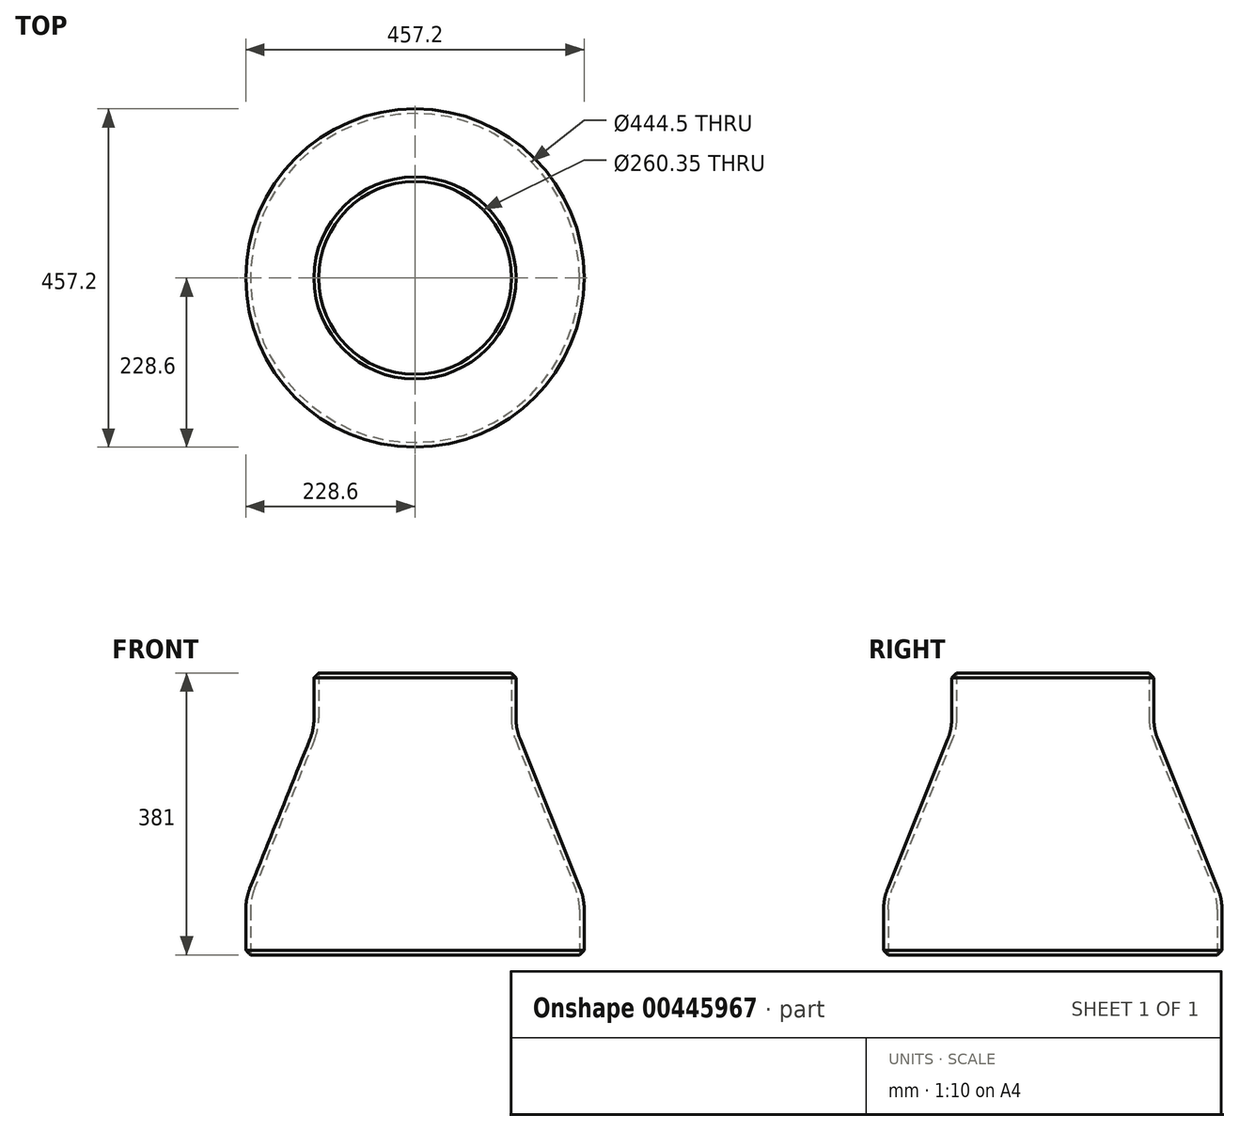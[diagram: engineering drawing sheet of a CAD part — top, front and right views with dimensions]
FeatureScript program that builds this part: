
annotation { "Feature Type Name" : "Feature", "Feature Type Description" : "" }
export const myFeature = defineFeature(function(context is Context, id is Id, definition is map)
    precondition{}
    {
        {
            var Q0;
            Q0=qCreatedBy(makeId("Front.planeOp"),FACE);
            var sketch = newSketch(context, id + "F0", { "sketchPlane" : qUnion([Q0])});
            skLineSegment(sketch, "E0", {"start": v(-130.18, 189.88) * mm, "end": v(-130.18, 128.45) * mm});
            skLineSegment(sketch, "E1", {"start": v(-222.25, -191.12) * mm, "end": v(-222.25, -129.68) * mm});
            skLineSegment(sketch, "E2", {"start": v(-216.73, -101.22) * mm, "end": v(-135.7, 99.98) * mm});
            skLineSegment(sketch, "E3", {"start": v(-136.53, 189.88) * mm, "end": v(-136.53, 128.45) * mm});
            skLineSegment(sketch, "E4", {"start": v(-142.04, 99.98) * mm, "end": v(-223.08, -101.22) * mm});
            skLineSegment(sketch, "E5", {"start": v(-228.6, -129.68) * mm, "end": v(-228.6, -191.12) * mm});
            skPoint(sketch, "E6.visualSharp", {"position": v(-222.25, -114.92) * mm});
            skArc(sketch, "E6.filletArc", {"start": v(-216.73, -101.22) * mm, "mid": v(-220.86, -115.19) * mm, "end": v(-222.25, -129.68) * mm});
            skPoint(sketch, "E7.visualSharp", {"position": v(-228.6, -114.92) * mm});
            skArc(sketch, "E7.filletArc", {"start": v(-223.08, -101.22) * mm, "mid": v(-227.2, -115.19) * mm, "end": v(-228.6, -129.68) * mm});
            skPoint(sketch, "E8.visualSharp", {"position": v(-136.53, 113.68) * mm});
            skArc(sketch, "E8.filletArc", {"start": v(-142.04, 99.98) * mm, "mid": v(-137.92, 113.95) * mm, "end": v(-136.53, 128.45) * mm});
            skPoint(sketch, "E9.visualSharp", {"position": v(-130.18, 113.68) * mm});
            skArc(sketch, "E9.filletArc", {"start": v(-135.7, 99.98) * mm, "mid": v(-131.57, 113.95) * mm, "end": v(-130.18, 128.45) * mm});
            skLineSegment(sketch, "E10", {"start": v(-136.53, 189.88) * mm, "end": v(-130.18, 189.88) * mm});
            skLineSegment(sketch, "E11", {"start": v(-228.6, -191.12) * mm, "end": v(-222.25, -191.12) * mm});
            skSolve(sketch);
        }
        {
            var Q0;
            Q0=qCreatedBy(makeId("Front.planeOp"),FACE);
            var sketch = newSketch(context, id + "F1", { "sketchPlane" : qUnion([Q0])});
            skLineSegment(sketch, "E12", {"start": v(0, 0) * mm, "end": v(0, 190.5) * mm});
            skLineSegment(sketch, "E13", {"start": v(0, 0) * mm, "end": v(0, -190.5) * mm});
            skSolve(sketch);
        }
        {
            var Q0;
            Q0=makeQuery(id+"F0.imprint","IMPRINT",FACE,{"disambiguationData":[TD([[makeQuery(id+"F0.imprint","IMPRINT",EDGE,{"derivedFrom":sQuery(id+"F0.wireOp",EDGE,"E0")}),-1.0]])]});
            var Q1;
            Q1=sQuery(id+"F1.wireOp",EDGE,"E12");
            revolve(context, id + "F2", {"entities" : qUnion([Q0]), "axis" : qUnion([Q1]), "revolveType" : RevolveType.FULL});
        }
        {
            var Q0;
            Q0=makeQuery(id+"F2.opRevolve","SWEPT_EDGE",EDGE,{"disambiguationData":[OSD([sQuery(id+"F0.wireOp",EDGE,"E3"),sQuery(id+"F0.wireOp",EDGE,"E10")])]});
            var Q1;
            Q1=makeQuery(id+"F2.opRevolve","SWEPT_EDGE",EDGE,{"disambiguationData":[OSD([sQuery(id+"F0.wireOp",EDGE,"E5"),sQuery(id+"F0.wireOp",EDGE,"E11")])]});
            chamfer(context, id + "F3", {"entities" : qUnion([Q0, Q1]), "width" : 6.35 * mm, "tangentPropagation" : true});
        }
    });
